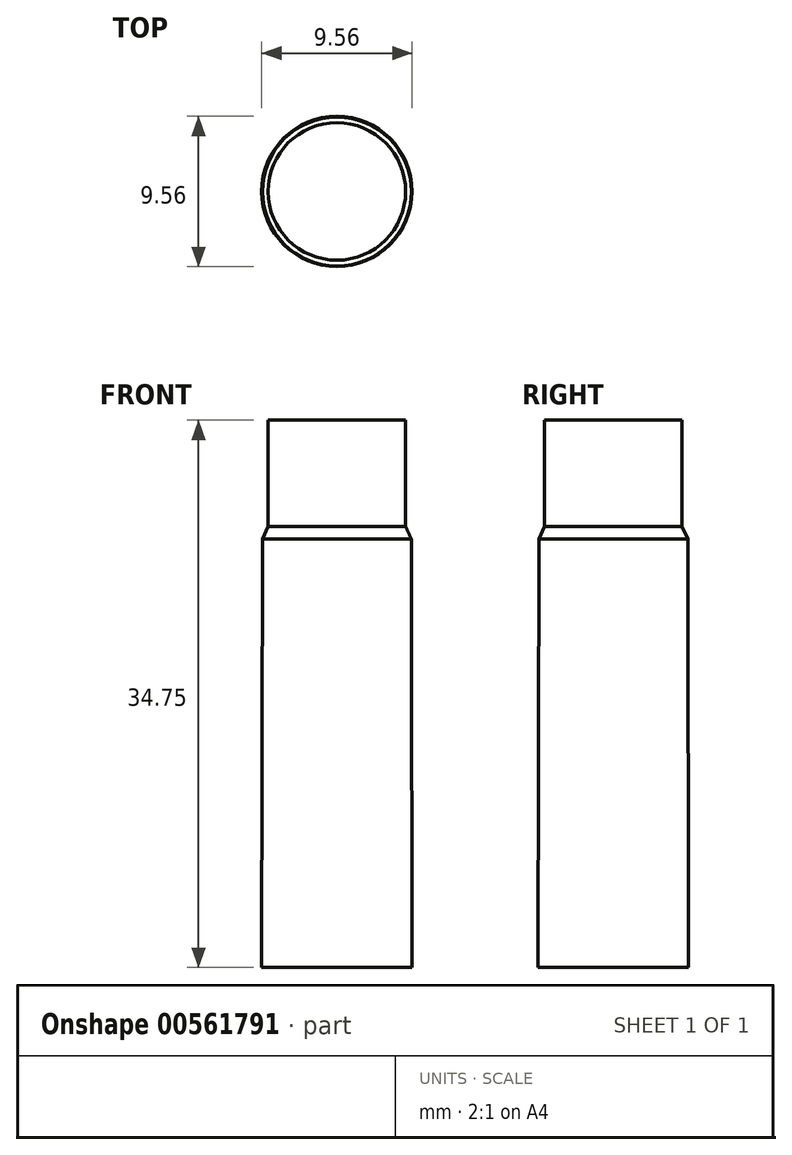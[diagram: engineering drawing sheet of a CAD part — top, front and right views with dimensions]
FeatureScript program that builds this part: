
annotation { "Feature Type Name" : "Feature", "Feature Type Description" : "" }
export const myFeature = defineFeature(function(context is Context, id is Id, definition is map)
    precondition{}
    {
        {
            var Q0;
            Q0=qCreatedBy(makeId("Front.planeOp"),FACE);
            var sketch = newSketch(context, id + "F0", { "sketchPlane" : qUnion([Q0])});
            skLineSegment(sketch, "E0", {"start": v(0, 0) * mm, "end": v(4.78, 0) * mm});
            skLineSegment(sketch, "E1", {"start": v(0, 27.2) * mm, "end": v(4.73, 27.2) * mm});
            skLineSegment(sketch, "E2", {"start": v(0, 28) * mm, "end": v(4.37, 28) * mm});
            skLineSegment(sketch, "E3", {"start": v(0, 34.75) * mm, "end": v(4.37, 34.75) * mm});
            skLineSegment(sketch, "E4", {"start": v(4.78, 0) * mm, "end": v(4.73, 27.2) * mm});
            skLineSegment(sketch, "E5", {"start": v(4.73, 27.2) * mm, "end": v(4.37, 28) * mm});
            skLineSegment(sketch, "E6", {"start": v(4.37, 28) * mm, "end": v(4.37, 34.75) * mm});
            skLineSegment(sketch, "E7", {"start": v(0, 34.75) * mm, "end": v(0, 0) * mm});
            skLineSegment(sketch, "E8.MirrorCS", {"start": v(-4.73, 27.2) * mm, "end": v(-4.37, 28) * mm});
            skLineSegment(sketch, "E9.MirrorCS", {"start": v(0, 27.2) * mm, "end": v(-4.73, 27.2) * mm});
            skLineSegment(sketch, "E10.MirrorCS", {"start": v(0, 0) * mm, "end": v(-4.78, 0) * mm});
            skLineSegment(sketch, "E11.MirrorCS", {"start": v(-4.37, 28) * mm, "end": v(-4.37, 34.75) * mm});
            skLineSegment(sketch, "E12.MirrorCS", {"start": v(0, 28) * mm, "end": v(-4.37, 28) * mm});
            skLineSegment(sketch, "E13.MirrorCS", {"start": v(0, 34.75) * mm, "end": v(-4.37, 34.75) * mm});
            skLineSegment(sketch, "E14.MirrorCS", {"start": v(-4.77, 0) * mm, "end": v(-4.73, 27.2) * mm});
            skSolve(sketch);
        }
        {
            var Q0;
            {var subQ0=sQuery(id+"F0.wireOp",EDGE,"E1");Q0=makeQuery(id+"F0.imprint","IMPRINT",FACE,{"disambiguationData":[TD([[makeQuery(id+"F0.imprint","IMPRINT",EDGE,{"derivedFrom":subQ0}),1.0]])]});}
            var Q1;
            {var subQ0=sQuery(id+"F0.wireOp",EDGE,"E2");Q1=makeQuery(id+"F0.imprint","IMPRINT",FACE,{"disambiguationData":[TD([[makeQuery(id+"F0.imprint","IMPRINT",EDGE,{"derivedFrom":subQ0}),1.0]])]});}
            var Q2;
            {var subQ0=sQuery(id+"F0.wireOp",EDGE,"E0");Q2=makeQuery(id+"F0.imprint","IMPRINT",FACE,{"disambiguationData":[TD([[makeQuery(id+"F0.imprint","IMPRINT",EDGE,{"derivedFrom":subQ0}),1.0]])]});}
            var Q3;
            Q3=sQuery(id+"F0.wireOp",EDGE,"E7");
            revolve(context, id + "F1", {"entities" : qUnion([Q0, Q1, Q2]), "axis" : qUnion([Q3]), "revolveType" : RevolveType.FULL});
        }
    });
